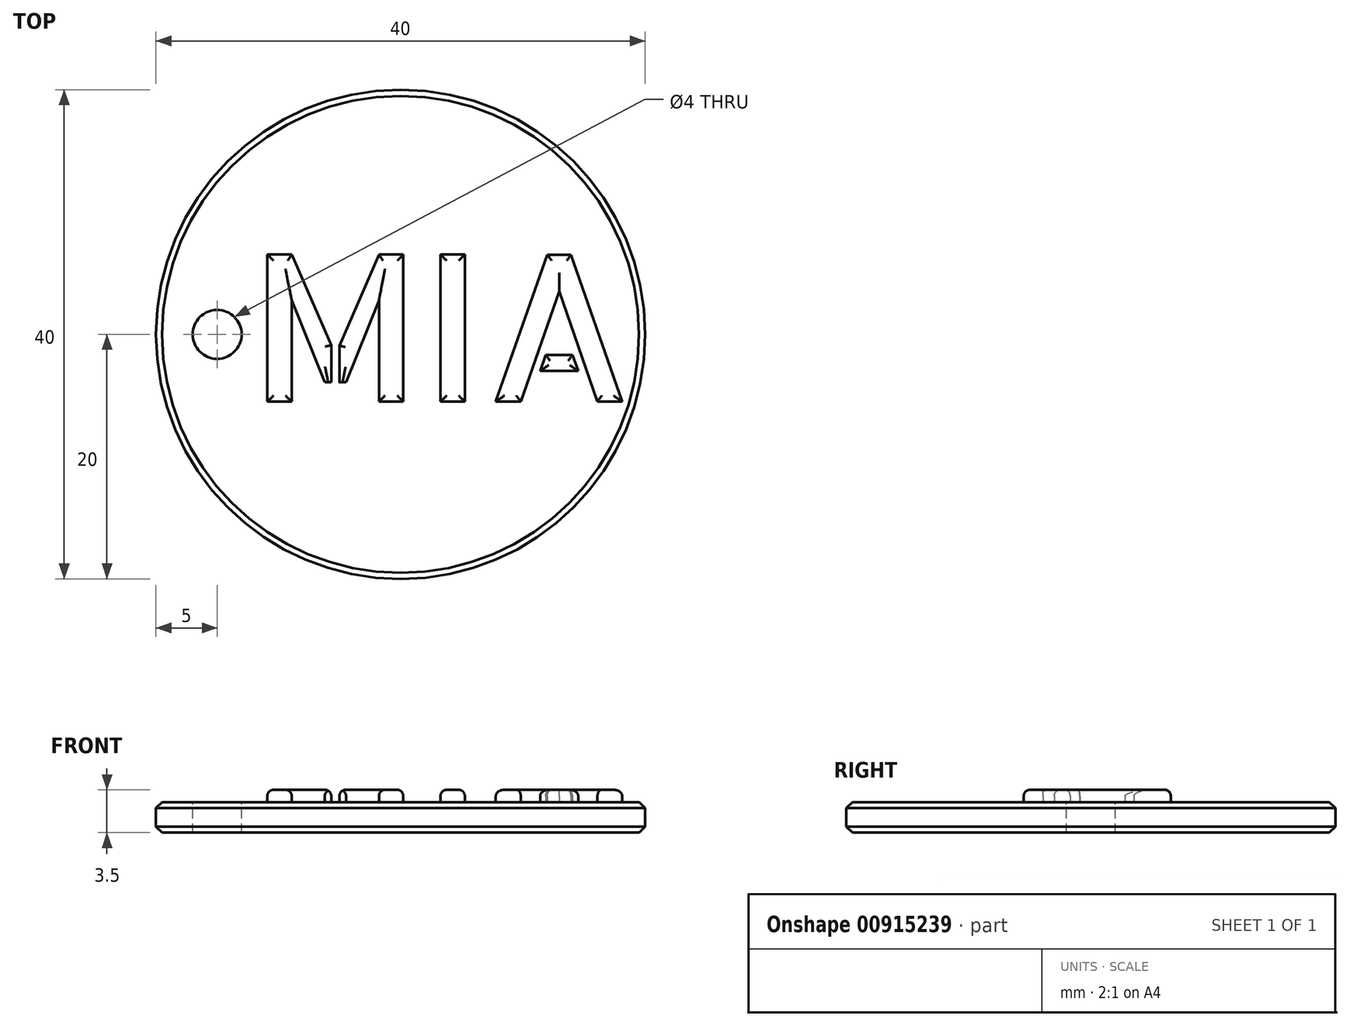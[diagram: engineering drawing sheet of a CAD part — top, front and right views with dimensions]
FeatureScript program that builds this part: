
annotation { "Feature Type Name" : "Feature", "Feature Type Description" : "" }
export const myFeature = defineFeature(function(context is Context, id is Id, definition is map)
    precondition{}
    {
        {
            var Q0;
            Q0=qCreatedBy(makeId("Top.planeOp"),FACE);
            var sketch = newSketch(context, id + "F0", { "sketchPlane" : qUnion([Q0])});
            skCircle(sketch, "E0", {"center": v(0, 0) * mm, "radius": 20 * mm});
            skSolve(sketch);
        }
        {
            var Q0;
            Q0=makeQuery(id+"F0.imprint","IMPRINT",FACE,{"disambiguationData":[TD([[makeQuery(id+"F0.imprint","IMPRINT",EDGE,{"derivedFrom":sQuery(id+"F0.wireOp",EDGE,"E0")}),1.0]])]});
            extrude(context, id + "F1", {"entities" : qUnion([Q0]), "depth" : 2.5 * mm, "offsetDistance" : 25 * mm});
        }
        {
            var Q0;
            Q0=makeQuery(id+"F1.opExtrude","CAP_FACE",FACE,{"disambiguationData":[OSD([sQuery(id+"F0.wireOp",EDGE,"E0")])],"isStart":false});
            var sketch = newSketch(context, id + "F2", { "sketchPlane" : qUnion([Q0])});
            skCircle(sketch, "E1", {"center": v(-15, 0) * mm, "radius": 2 * mm});
            skLineSegment(sketch, "E2", {"start": v(-15, 0) * mm, "end": v(0, 0) * mm, "construction": true});
            skSolve(sketch);
        }
        {
            var Q0;
            Q0 = qSketchRegion(id + "F2", true);
            extrude(context, id + "F3", {"entities" : qUnion([Q0]), "operationType" : NewBodyOperationType.REMOVE, "endBound" : BoundingType.THROUGH_ALL, "oppositeDirection" : true, "depth" : 25 * mm, "offsetDistance" : 25 * mm});
        }
        {
            var Q0;
            Q0=makeQuery(id+"F1.opExtrude","CAP_FACE",FACE,{"disambiguationData":[OSD([sQuery(id+"F0.wireOp",EDGE,"E0")])],"isStart":false});
            var sketch = newSketch(context, id + "F4", { "sketchPlane" : qUnion([Q0])});
            skText(sketch, "E3", { "text": "MIA", "fontName": "AllertaStencil-Regular.ttf"});
            const initialGuessF4  = {"E3": [-0.0124, -0.0055, 1, 0, 0.01204]};
            skSetInitialGuess(sketch, initialGuessF4);
            skSolve(sketch);
        }
        {
            var Q0;
            Q0 = qSketchRegion(id + "F4", true);
            extrude(context, id + "F5", {"entities" : qUnion([Q0]), "operationType" : NewBodyOperationType.ADD, "depth" : 1 * mm, "offsetDistance" : 25 * mm});
        }
        {
            var Q0;
            Q0=makeQuery(id+"F1.opExtrude","CAP_EDGE",EDGE,{"disambiguationData":[OSD([sQuery(id+"F0.wireOp",EDGE,"E0")])],"isStart":false});
            var Q1;
            Q1=makeQuery(id+"F1.opExtrude","CAP_EDGE",EDGE,{"disambiguationData":[OSD([sQuery(id+"F0.wireOp",EDGE,"E0")])],"isStart":true});
            chamfer(context, id + "F6", {"entities" : qUnion([Q0, Q1]), "width" : 0.5 * mm, "tangentPropagation" : true});
        }
        {
            var Q0;
            Q0=makeQuery(id+"F5.opExtrude","CAP_FACE",FACE,{"disambiguationData":[OSD([sQuery(id+"F4.wireOp",EDGE,"E3.sketch_text.stroke-0"),sQuery(id+"F4.wireOp",EDGE,"E3.sketch_text.stroke-1"),sQuery(id+"F4.wireOp",EDGE,"E3.sketch_text.stroke-2"),sQuery(id+"F4.wireOp",EDGE,"E3.sketch_text.stroke-3"),sQuery(id+"F4.wireOp",EDGE,"E3.sketch_text.stroke-4"),sQuery(id+"F4.wireOp",EDGE,"E3.sketch_text.stroke-5"),sQuery(id+"F4.wireOp",EDGE,"E3.sketch_text.stroke-6"),sQuery(id+"F4.wireOp",EDGE,"E3.sketch_text.stroke-7")])],"isStart":false});
            var Q1;
            Q1=makeQuery(id+"F5.opExtrude","CAP_FACE",FACE,{"disambiguationData":[OSD([sQuery(id+"F4.wireOp",EDGE,"E3.sketch_text.stroke-8"),sQuery(id+"F4.wireOp",EDGE,"E3.sketch_text.stroke-9"),sQuery(id+"F4.wireOp",EDGE,"E3.sketch_text.stroke-10"),sQuery(id+"F4.wireOp",EDGE,"E3.sketch_text.stroke-11"),sQuery(id+"F4.wireOp",EDGE,"E3.sketch_text.stroke-12"),sQuery(id+"F4.wireOp",EDGE,"E3.sketch_text.stroke-13"),sQuery(id+"F4.wireOp",EDGE,"E3.sketch_text.stroke-14"),sQuery(id+"F4.wireOp",EDGE,"E3.sketch_text.stroke-15")])],"isStart":false});
            var Q2;
            Q2=makeQuery(id+"F5.opExtrude","CAP_FACE",FACE,{"disambiguationData":[OSD([sQuery(id+"F4.wireOp",EDGE,"E3.sketch_text.stroke-16"),sQuery(id+"F4.wireOp",EDGE,"E3.sketch_text.stroke-17"),sQuery(id+"F4.wireOp",EDGE,"E3.sketch_text.stroke-18"),sQuery(id+"F4.wireOp",EDGE,"E3.sketch_text.stroke-19")])],"isStart":false});
            var Q3;
            Q3=makeQuery(id+"F5.opExtrude","CAP_EDGE",EDGE,{"disambiguationData":[OSD([sQuery(id+"F4.wireOp",EDGE,"E3.sketch_text.stroke-22")])],"isStart":false});
            var Q4;
            Q4=makeQuery(id+"F5.opExtrude","CAP_FACE",FACE,{"disambiguationData":[OSD([sQuery(id+"F4.wireOp",EDGE,"E3.sketch_text.stroke-20"),sQuery(id+"F4.wireOp",EDGE,"E3.sketch_text.stroke-21"),sQuery(id+"F4.wireOp",EDGE,"E3.sketch_text.stroke-22"),sQuery(id+"F4.wireOp",EDGE,"E3.sketch_text.stroke-23"),sQuery(id+"F4.wireOp",EDGE,"E3.sketch_text.stroke-24"),sQuery(id+"F4.wireOp",EDGE,"E3.sketch_text.stroke-25"),sQuery(id+"F4.wireOp",EDGE,"E3.sketch_text.stroke-26")])],"isStart":false});
            var Q5;
            Q5=makeQuery(id+"F5.opExtrude","CAP_FACE",FACE,{"disambiguationData":[OSD([sQuery(id+"F4.wireOp",EDGE,"E3.sketch_text.stroke-27"),sQuery(id+"F4.wireOp",EDGE,"E3.sketch_text.stroke-28"),sQuery(id+"F4.wireOp",EDGE,"E3.sketch_text.stroke-29"),sQuery(id+"F4.wireOp",EDGE,"E3.sketch_text.stroke-30")])],"isStart":false});
            fillet(context, id + "F7", {"entities" : qUnion([Q0, Q1, Q2, Q3, Q4, Q5]), "radius" : 0.5 * mm, "tangentPropagation" : true, "allowEdgeOverflow" : false});
        }
    });
